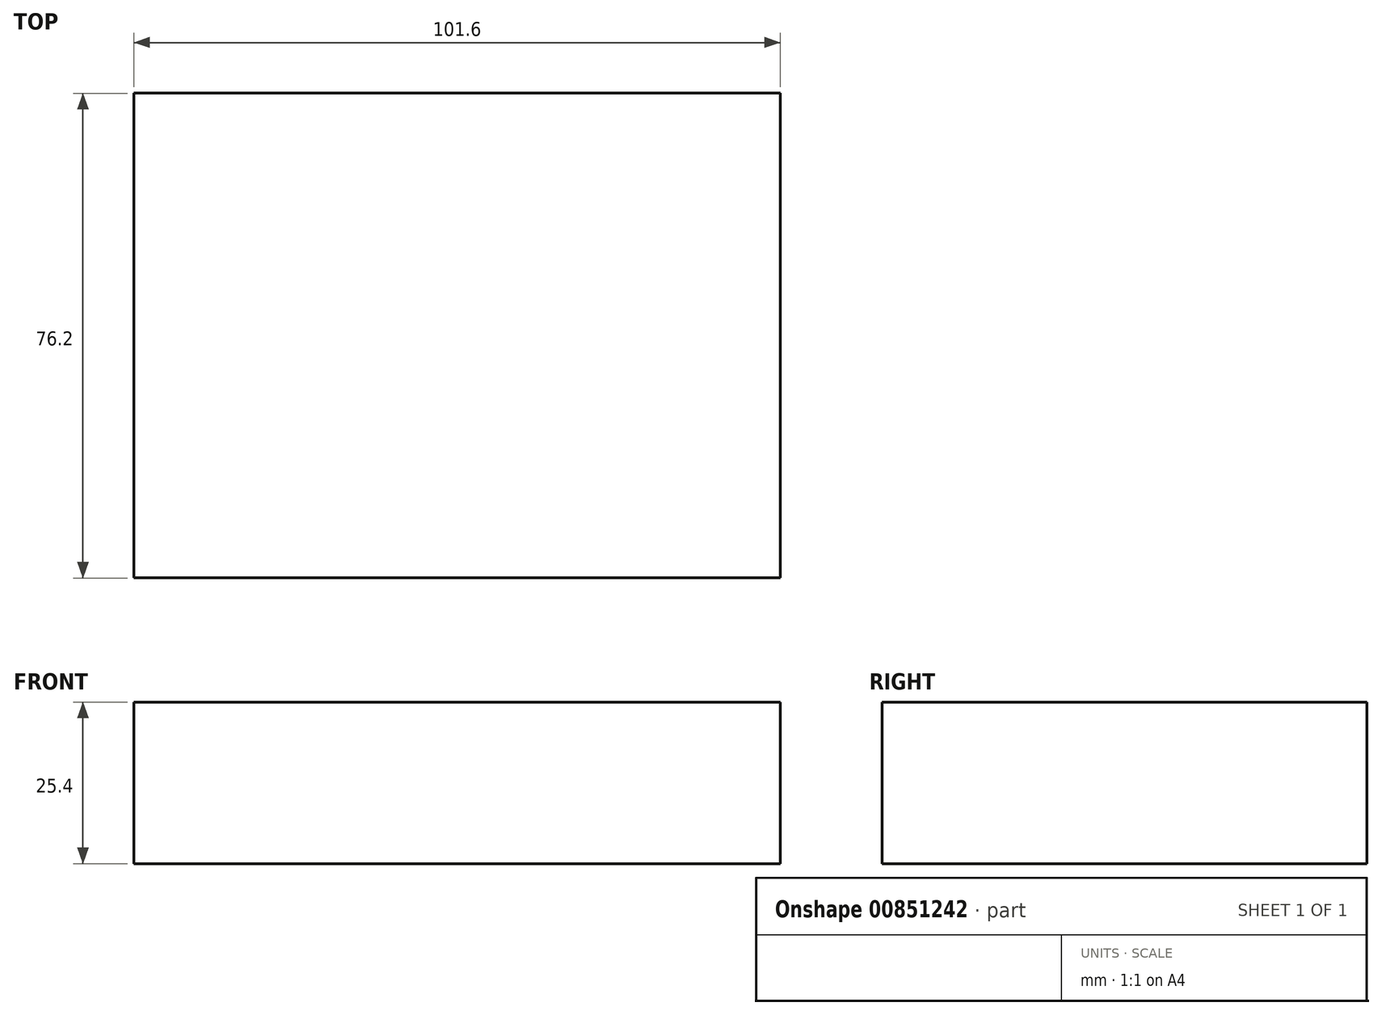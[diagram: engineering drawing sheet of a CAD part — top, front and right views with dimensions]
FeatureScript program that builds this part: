
annotation { "Feature Type Name" : "Feature", "Feature Type Description" : "" }
export const myFeature = defineFeature(function(context is Context, id is Id, definition is map)
    precondition{}
    {
        {
            var Q0;
            Q0=qCreatedBy(makeId("Top.planeOp"),FACE);
            var sketch = newSketch(context, id + "F0", { "sketchPlane" : qUnion([Q0])});
            skLineSegment(sketch, "E0.bottom", {"start": v(-36.93, 29.1) * mm, "end": v(64.67, 29.1) * mm});
            skLineSegment(sketch, "E0.top", {"start": v(-36.93, -47.1) * mm, "end": v(64.67, -47.1) * mm});
            skLineSegment(sketch, "E0.left", {"start": v(-36.93, 29.1) * mm, "end": v(-36.93, -47.1) * mm});
            skLineSegment(sketch, "E0.right", {"start": v(64.67, 29.1) * mm, "end": v(64.67, -47.1) * mm});
            skSolve(sketch);
        }
        {
            var Q0;
            Q0=makeQuery(id+"F0.imprint","IMPRINT",FACE,{"disambiguationData":[TD([[makeQuery(id+"F0.imprint","IMPRINT",EDGE,{"derivedFrom":sQuery(id+"F0.wireOp",EDGE,"E0.bottom")}),-1.0]])]});
            extrude(context, id + "F1", {"entities" : qUnion([Q0]), "depth" : 25.4 * mm, "offsetDistance" : 25.4 * mm});
        }
    });
